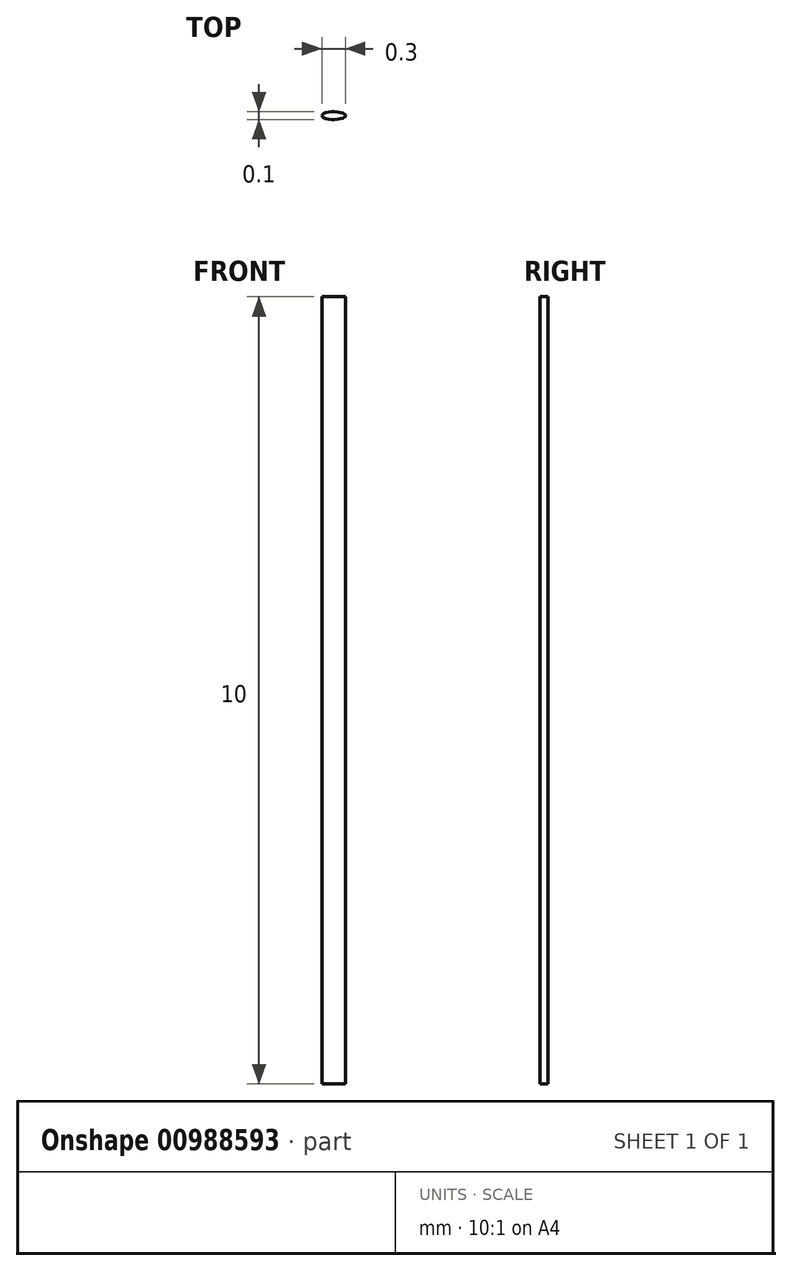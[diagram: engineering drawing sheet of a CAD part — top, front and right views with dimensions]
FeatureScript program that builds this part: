
annotation { "Feature Type Name" : "Feature", "Feature Type Description" : "" }
export const myFeature = defineFeature(function(context is Context, id is Id, definition is map)
    precondition{}
    {
        {
            var Q0;
            Q0=qCreatedBy(makeId("Top.planeOp"),FACE);
            var sketch = newSketch(context, id + "F0", { "sketchPlane" : qUnion([Q0])});
            skEllipse(sketch, "E0", {"center": v(0, 0) * mm, "majorRadius": 0.05 * mm, "minorRadius": 0.15 * mm, "majorAxis": v(0, 1)});
            skSolve(sketch);
        }
        {
            var Q0;
            Q0=makeQuery(id+"F0.imprint","IMPRINT",FACE,{"disambiguationData":[TD([[makeQuery(id+"F0.imprint","IMPRINT",EDGE,{"derivedFrom":sQuery(id+"F0.wireOp",EDGE,"E0")}),1.0]])]});
            extrude(context, id + "F1", {"entities" : qUnion([Q0]), "depth" : 10 * mm, "offsetDistance" : 25 * mm});
        }
    });
